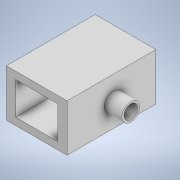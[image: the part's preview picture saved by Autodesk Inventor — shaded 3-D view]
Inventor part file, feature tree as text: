
AUTODESK INVENTOR PART (.ipt)
format: ipt  version: 2020.3 (Build 243373000, 373)  size: 104,448 bytes
history: native  units: mm
features: extrude x2, sketch x2
ambient origin geometry x8: Origin, YZ Plane, XZ Plane, XY Plane, X Axis, Y Axis, Z Axis, Center Point
bodies: Solid1 (feature_tree)
feature tree (4):
  extrude  "Extrusion1"  Depth=2.0mm TaperAngle=0.0deg
  extrude  "Extrusion2"  [1 undecoded]
  sketch  "Sketch1"  dims[d0=10.0mm d1=0.0mm d2=2.0mm d3=0.0mm]
  sketch  "Sketch2"
note: 1 required parameter value undecoded (feature->parameter linkage not recoverable at this tier; creation-order binding heuristic only, values carry confidence <= 0.55)
